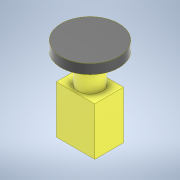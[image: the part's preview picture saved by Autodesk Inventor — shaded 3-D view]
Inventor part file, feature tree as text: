
AUTODESK INVENTOR PART (.ipt)
format: ipt  version: 2021 (Build 250183000, 183)  size: 118,272 bytes
history: native  units: in
note: dims shown in document units (in); Inventor stores cm internally (conversion verified against a paired STEP export)
features: extrude x3, sketch x3
ambient origin geometry x8: Origin, YZ Plane, XZ Plane, XY Plane, X Axis, Y Axis, Z Axis, Center Point
bodies: Solid1 (feature_tree)
feature tree (6):
  extrude  "Extrusion1"  Depth=3.0in
  extrude  "Extrusion2"  Depth=2.5in
  extrude  "Extrusion3"  Depth=1.0in
  sketch  "Sketch1"  dims[d0=4.0in d1=3.0in]
  sketch  "Sketch2"  dims[d2=5.0in d3=0.0in d4=2.5in]
  sketch  "Sketch3"  dims[d5=3.0in d6=0.0in d7=6.0in d8=1.0in d9=0.0in]
